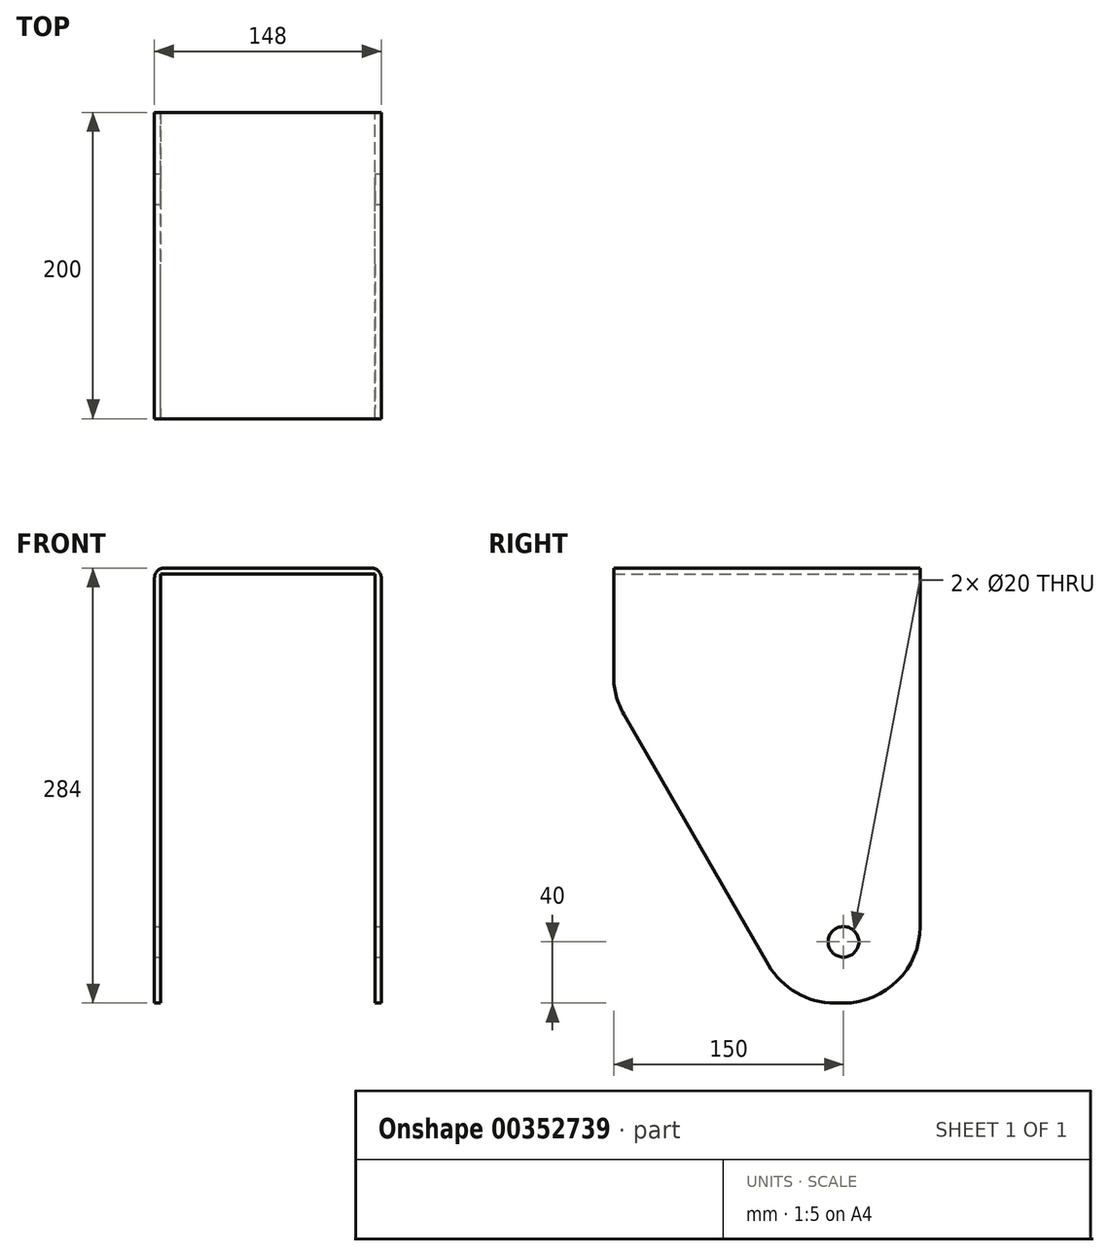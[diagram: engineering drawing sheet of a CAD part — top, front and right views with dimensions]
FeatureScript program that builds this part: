
annotation { "Feature Type Name" : "Feature", "Feature Type Description" : "" }
export const myFeature = defineFeature(function(context is Context, id is Id, definition is map)
    precondition{}
    {
        {
            var Q0;
            Q0=qCreatedBy(makeId("Front.planeOp"),FACE);
            var sketch = newSketch(context, id + "F0", { "sketchPlane" : qUnion([Q0])});
            skLineSegment(sketch, "E0", {"start": v(-72, 0) * mm, "end": v(-72, 277.65) * mm});
            skLineSegment(sketch, "E1", {"start": v(-65.65, 284) * mm, "end": v(69.65, 284) * mm});
            skLineSegment(sketch, "E2", {"start": v(76, 277.65) * mm, "end": v(76, 0) * mm});
            skPoint(sketch, "E3.visualSharp", {"position": v(-72, 284) * mm});
            skArc(sketch, "E3.filletArc", {"start": v(-65.65, 284) * mm, "mid": v(-70.14, 282.14) * mm, "end": v(-72, 277.65) * mm});
            skPoint(sketch, "E4.visualSharp", {"position": v(76, 284) * mm});
            skArc(sketch, "E4.filletArc", {"start": v(76, 277.65) * mm, "mid": v(74.14, 282.14) * mm, "end": v(69.65, 284) * mm});
            skLineSegment(sketch, "E5.0", {"start": v(72, 280) * mm, "end": v(72, 0) * mm});
            skLineSegment(sketch, "E5.1", {"start": v(-68, 280) * mm, "end": v(72, 280) * mm});
            skLineSegment(sketch, "E5.2", {"start": v(-68, 0) * mm, "end": v(-68, 280) * mm});
            skLineSegment(sketch, "E6", {"start": v(-72, 0) * mm, "end": v(-68, 0) * mm});
            skLineSegment(sketch, "E7", {"start": v(72, 0) * mm, "end": v(76, 0) * mm});
            skSolve(sketch);
        }
        {
            var Q0;
            Q0 = qSketchRegion(id + "F0", true);
            extrude(context, id + "F1", {"entities" : qUnion([Q0]), "endBound" : BoundingType.SYMMETRIC, "depth" : 200 * mm});
        }
        {
            var Q0;
            Q0=makeQuery(id+"F1.opExtrude","CAP_EDGE",EDGE,{"disambiguationData":[OSD([sQuery(id+"F0.wireOp",EDGE,"E7")])],"isStart":false});
            var Q1;
            Q1=makeQuery(id+"F1.opExtrude","CAP_EDGE",EDGE,{"disambiguationData":[OSD([sQuery(id+"F0.wireOp",EDGE,"E6")])],"isStart":false});
            chamfer(context, id + "F2", {"entities" : qUnion([Q0, Q1]), "chamferType" : ChamferType.OFFSET_ANGLE, "width" : 200 * mm, "oppositeDirection" : false, "angle" : 30 * degree, "tangentPropagation" : true});
        }
        {
            var Q0;
            {var subQ0=sQuery(id+"F0.wireOp",EDGE,"E7");Q0=makeQuery(id+"F2.opChamfer","BLEND_EDGE",EDGE,{"blendedFrom":[makeQuery(id+"F1.opExtrude","CAP_EDGE",EDGE,{"disambiguationData":[OSD([subQ0])],"isStart":false}),makeQuery(id+"F1.opExtrude","CAP_FACE",FACE,{"disambiguationData":[OSD([sQuery(id+"F0.wireOp",EDGE,"E0"),sQuery(id+"F0.wireOp",EDGE,"E1"),sQuery(id+"F0.wireOp",EDGE,"E2"),sQuery(id+"F0.wireOp",EDGE,"E3.filletArc"),sQuery(id+"F0.wireOp",EDGE,"E4.filletArc"),sQuery(id+"F0.wireOp",EDGE,"E5.0"),sQuery(id+"F0.wireOp",EDGE,"E5.1"),sQuery(id+"F0.wireOp",EDGE,"E5.2"),sQuery(id+"F0.wireOp",EDGE,"E6"),subQ0])],"isStart":false})],"blendedInto":[makeQuery(id+"F1.opExtrude","CAP_FACE",FACE,{"disambiguationData":[OSD([sQuery(id+"F0.wireOp",EDGE,"E0"),sQuery(id+"F0.wireOp",EDGE,"E1"),sQuery(id+"F0.wireOp",EDGE,"E2"),sQuery(id+"F0.wireOp",EDGE,"E3.filletArc"),sQuery(id+"F0.wireOp",EDGE,"E4.filletArc"),sQuery(id+"F0.wireOp",EDGE,"E5.0"),sQuery(id+"F0.wireOp",EDGE,"E5.1"),sQuery(id+"F0.wireOp",EDGE,"E5.2"),sQuery(id+"F0.wireOp",EDGE,"E6"),subQ0])],"isStart":false})]});}
            var Q1;
            {var subQ0=sQuery(id+"F0.wireOp",EDGE,"E6");Q1=makeQuery(id+"F2.opChamfer","BLEND_EDGE",EDGE,{"blendedFrom":[makeQuery(id+"F1.opExtrude","CAP_EDGE",EDGE,{"disambiguationData":[OSD([subQ0])],"isStart":false}),makeQuery(id+"F1.opExtrude","CAP_FACE",FACE,{"disambiguationData":[OSD([sQuery(id+"F0.wireOp",EDGE,"E0"),sQuery(id+"F0.wireOp",EDGE,"E1"),sQuery(id+"F0.wireOp",EDGE,"E2"),sQuery(id+"F0.wireOp",EDGE,"E3.filletArc"),sQuery(id+"F0.wireOp",EDGE,"E4.filletArc"),sQuery(id+"F0.wireOp",EDGE,"E5.0"),sQuery(id+"F0.wireOp",EDGE,"E5.1"),sQuery(id+"F0.wireOp",EDGE,"E5.2"),subQ0,sQuery(id+"F0.wireOp",EDGE,"E7")])],"isStart":false})],"blendedInto":[makeQuery(id+"F1.opExtrude","CAP_FACE",FACE,{"disambiguationData":[OSD([sQuery(id+"F0.wireOp",EDGE,"E0"),sQuery(id+"F0.wireOp",EDGE,"E1"),sQuery(id+"F0.wireOp",EDGE,"E2"),sQuery(id+"F0.wireOp",EDGE,"E3.filletArc"),sQuery(id+"F0.wireOp",EDGE,"E4.filletArc"),sQuery(id+"F0.wireOp",EDGE,"E5.0"),sQuery(id+"F0.wireOp",EDGE,"E5.1"),sQuery(id+"F0.wireOp",EDGE,"E5.2"),subQ0,sQuery(id+"F0.wireOp",EDGE,"E7")])],"isStart":false})]});}
            var Q2;
            {var subQ0=sQuery(id+"F0.wireOp",EDGE,"E7");Q2=makeQuery(id+"F2.opChamfer","BLEND_EDGE",EDGE,{"blendedFrom":[makeQuery(id+"F1.opExtrude","CAP_EDGE",EDGE,{"disambiguationData":[OSD([subQ0])],"isStart":false}),makeQuery(id+"F1.opExtrude","SWEPT_FACE",FACE,{"disambiguationData":[OSD([subQ0])]})],"blendedInto":[makeQuery(id+"F1.opExtrude","SWEPT_FACE",FACE,{"disambiguationData":[OSD([subQ0])]})]});}
            var Q3;
            {var subQ0=sQuery(id+"F0.wireOp",EDGE,"E6");Q3=makeQuery(id+"F2.opChamfer","BLEND_EDGE",EDGE,{"blendedFrom":[makeQuery(id+"F1.opExtrude","CAP_EDGE",EDGE,{"disambiguationData":[OSD([subQ0])],"isStart":false}),makeQuery(id+"F1.opExtrude","SWEPT_FACE",FACE,{"disambiguationData":[OSD([subQ0])]})],"blendedInto":[makeQuery(id+"F1.opExtrude","SWEPT_FACE",FACE,{"disambiguationData":[OSD([subQ0])]})]});}
            var Q4;
            Q4=makeQuery(id+"F1.opExtrude","CAP_EDGE",EDGE,{"disambiguationData":[OSD([sQuery(id+"F0.wireOp",EDGE,"E6")])],"isStart":true});
            var Q5;
            Q5=makeQuery(id+"F1.opExtrude","CAP_EDGE",EDGE,{"disambiguationData":[OSD([sQuery(id+"F0.wireOp",EDGE,"E7")])],"isStart":true});
            fillet(context, id + "F3", {"entities" : qUnion([Q0, Q1, Q2, Q3, Q4, Q5]), "radius" : 50 * mm, "tangentPropagation" : true, "allowEdgeOverflow" : false});
        }
        {
            var Q0;
            Q0=qCreatedBy(makeId("Right.planeOp"),FACE);
            var sketch = newSketch(context, id + "F4", { "sketchPlane" : qUnion([Q0])});
            skCircle(sketch, "E8", {"center": v(50, 40) * mm, "radius": 10 * mm});
            skSolve(sketch);
        }
        {
            var Q0;
            Q0 = qSketchRegion(id + "F4", true);
            extrude(context, id + "F5", {"entities" : qUnion([Q0]), "operationType" : NewBodyOperationType.REMOVE, "endBound" : BoundingType.SYMMETRIC, "oppositeDirection" : true, "depth" : 200 * mm});
        }
    });
